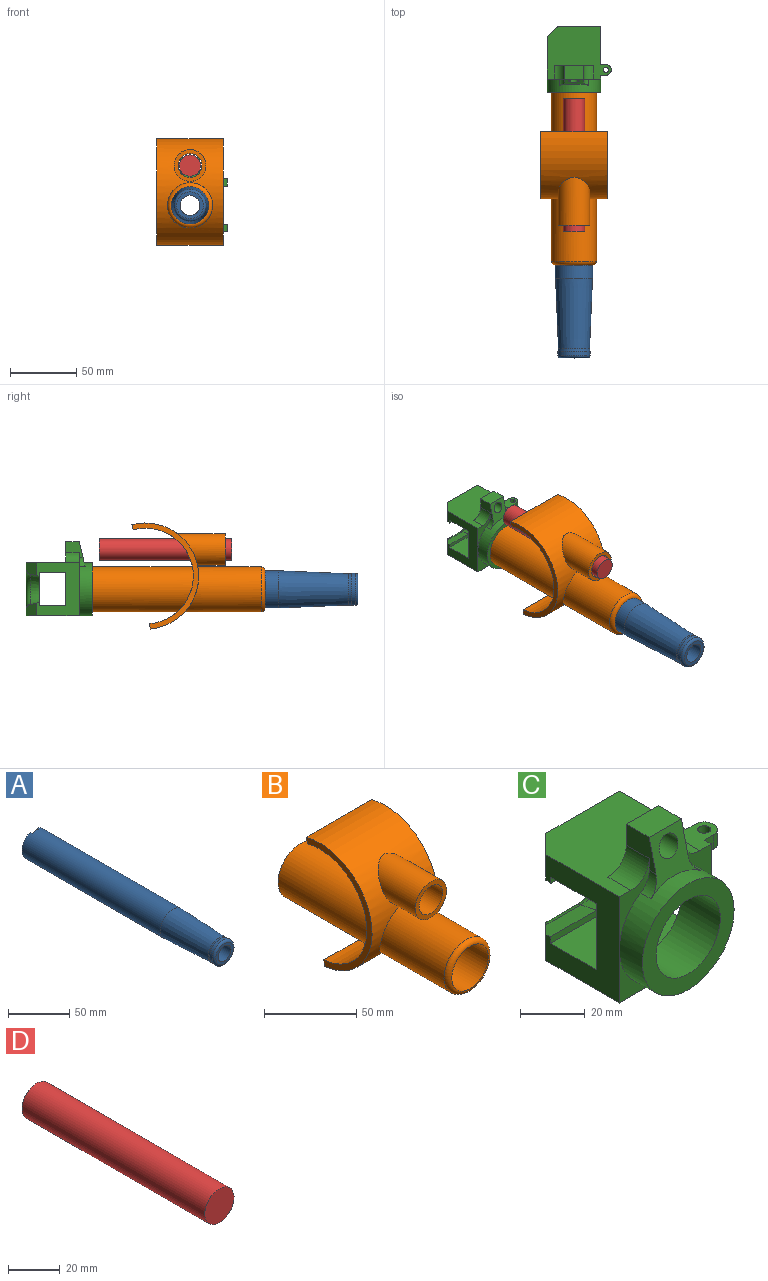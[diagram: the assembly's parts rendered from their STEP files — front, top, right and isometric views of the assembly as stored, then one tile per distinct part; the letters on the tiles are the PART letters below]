
ASSEMBLY  parts=4 mates=3
PART A: 19 faces, bbox 28.7x220x28.7 mm
  f0: plane 26.83x10mm, normal (0,1,0), area 139.7mm2, adj f1,f2,f14,f17
  f1: cylinder r=14mm len=160mm, axis (0,1,0), area 14041.9mm2, adj f0,f3,f4,f13,f14,f15,f16,f17
  f2: cylinder r=9mm len=30mm, axis (0,1,0), area 1663.3mm2, adj f0,f4,f8,f13,f14,f15,f16,f17
  f3: cone r=14mm half-angle=2.4deg, axis (0,1,0), area 4301.6mm2, adj f1,f11
  f4: plane 26.83x10mm, normal (0,1,0), area 139.7mm2, adj f1,f2,f15,f16
  f5: plane 20.2x20.2mm, normal (0,-1,0), area 143.8mm2, adj f6,f12
  f6: cylinder r=7.5mm len=175mm, axis (0,1,0), area 8246.7mm2, adj f5,f10
  f7: cylinder r=12.1mm len=24.2mm, axis (0,-1,0), area 228.1mm2, adj f11,f12
  f8: cone r=9mm half-angle=6.7deg, axis (0,1,0), area 630mm2, adj f2,f9
  f9: cylinder r=7.6mm len=15.2mm, axis (0,1,0), area 143.3mm2, adj f8,f10
  f10: plane 15.2x15.2mm, normal (0,1,0), area 4.7mm2, adj f6,f9
  f11: torus R=16.79mm, axis (0,-1,0), area 148.6mm2, adj f3,f7
  f12: torus R=10.1mm, axis (0,-1,0), area 224.5mm2, adj f5,f7
  f13: plane 8x5.94mm, normal (0,1,0), area 40.9mm2, adj f1,f2,f14,f15
  f14: plane 5.35x2mm, normal (-1,0,0), area 10.7mm2, adj f0,f1,f2,f13
  f15: plane 5.35x2mm, normal (1,0,0), area 10.7mm2, adj f1,f2,f4,f13
  f16: plane 5.35x2mm, normal (1,0,0), area 10.7mm2, adj f1,f2,f4,f18
  f17: plane 5.35x2mm, normal (-1,0,0), area 10.7mm2, adj f0,f1,f2,f18
  f18: plane 8x5.94mm, normal (0,1,0), area 40.9mm2, adj f1,f2,f16,f17
PART B: 14 faces, bbox 50x130x79.8 mm
  f0: cylinder r=17mm len=57.49mm, axis (0,1,0), area 5380.1mm2, adj f1,f2
  f1: torus R=14mm, axis (0,-1,0), area 471.1mm2, adj f0,f12
  f2: cylinder r=40mm len=79.85mm, axis (-1,0,0), area 5123mm2, adj f0,f4,f5,f6,f7,f10
  f3: cylinder r=36mm len=71.86mm, axis (-1,0,0), area 4666.7mm2, adj f4,f5,f6,f7,f9,f13
  f4: plane 50x3.86mm, normal (0,0.97,-0.26), area 200mm2, adj f2,f3,f6,f7
  f5: plane 50x3.98mm, normal (0,1,-0.09), area 200mm2, adj f2,f3,f6,f7
  f6: plane 79.85x50.35mm, normal (1,0,0), area 504.1mm2, adj f2,f3,f4,f5
  f7: plane 79.85x50.35mm, normal (-1,0,0), area 504.1mm2, adj f2,f3,f4,f5
  f8: plane 34x34mm, normal (0,1,0), area 292.2mm2, adj f9,f12
  f9: cylinder r=17mm len=76mm, axis (0,1,0), area 7705.6mm2, adj f3,f8
  f10: cylinder r=12mm len=36mm, axis (0,-1,0), area 2024mm2, adj f2,f11
  f11: plane 24x24mm, normal (0,-1,0), area 197.9mm2, adj f10,f13
  f12: cylinder r=14mm len=130mm, axis (0,1,0), area 11435.4mm2, adj f1,f8
  f13: cylinder r=9mm len=38.67mm, axis (0,-1,0), area 1759.1mm2, adj f3,f11
PART C: 52 faces, bbox 48x50x56 mm
  f0: plane 40x29mm, normal (1,0,0), area 652.1mm2, adj f4,f5,f8,f13,f14,f24,f37,f41
  f1: plane 40x7mm, normal (1,0,0), area 236mm2, adj f8,f11,f12,f13,f37,f39,f41,f44
  f2: plane 3.3x1.17mm, normal (0,-1,0), area 2.2mm2, adj f5,f6,f38
  f3: plane 3.3x1.17mm, normal (0,-1,0), area 2.2mm2, adj f4,f6,f40
  f4: plane 40x20mm, normal (0,0,1), area 587.8mm2, adj f0,f3,f10,f17,f24,f40,f42
  f5: plane 40x20mm, normal (0,0,-1), area 587.8mm2, adj f0,f2,f10,f17,f24,f38,f43
  f6: cylinder r=14mm len=28mm, axis (0,-1,0), area 1609.2mm2, adj f2,f3,f16,f17,f38,f39,f40
  f7: plane 28x13mm, normal (0,-1,0), area 93mm2, adj f8,f9,f10,f28,f31,f33
  f8: plane 48x40mm, normal (0,0,1), area 1312.6mm2, adj f0,f1,f7,f10,f12,f14,f25,f31
  f9: cylinder r=20mm len=40mm, axis (0,1,0), area 1164.8mm2, adj f7,f11,f12,f15,f16,f27,f33,f34
  f10: plane 40x32mm, normal (-1,0,0), area 739.2mm2, adj f4,f5,f7,f8,f13,f15,f17,f18
  f11: plane 20x20mm, normal (0,-1,0), area 85.8mm2, adj f1,f9,f13
  f12: plane 28x13mm, normal (0,-1,0), area 93mm2, adj f1,f8,f9,f29,f32,f34
  f13: plane 48x40mm, normal (0,0,-1), area 1612.6mm2, adj f0,f1,f10,f11,f14,f15,f35,f48
  f14: plane 40x32mm, normal (0,1,0), area 546.6mm2, adj f0,f8,f13,f21,f22,f23,f35,f36
  f15: plane 20x20mm, normal (0,-1,0), area 85.8mm2, adj f9,f10,f13
  f16: plane 40x40mm, normal (0,-1,0), area 640.9mm2, adj f6,f9
  f17: plane 25x13.7mm, normal (0,1,0), area 204.9mm2, adj f4,f5,f6,f10
  f18: plane 20x6.78mm, normal (0,0.2,0.98), area 126.7mm2, adj f10,f19,f23,f24,f35
  f19: cone r=10mm half-angle=11.3deg, axis (0,1,0), area 232.1mm2, adj f18,f20,f22,f24
  f20: plane 20x6.78mm, normal (0,0.2,-0.98), area 126.7mm2, adj f10,f19,f21,f24,f36
  f21: cylinder r=4mm len=15.22mm, axis (1,0,0), area 72.2mm2, adj f14,f20,f22,f36
  f22: torus R=15.28mm, axis (0,-1,0), area 223.3mm2, adj f14,f19,f21,f23
  f23: cylinder r=4mm len=15.22mm, axis (-1,0,0), area 72.2mm2, adj f14,f18,f22,f35
  f24: plane 40x25mm, normal (0,-1,0), area 442.9mm2, adj f0,f4,f5,f10,f18,f19,f20
  f25: plane 30x16mm, normal (0,1,0), area 201.2mm2, adj f8,f26,f28,f29,f30,f31,f32
  f26: plane 14x10mm, normal (0,0,1), area 140mm2, adj f25,f27,f28,f29
  f27: plane 21.43x19.11mm, normal (0,-0.97,0.23), area 192.1mm2, adj f9,f26,f28,f29,f30,f33,f34
  f28: plane 12.94x12.36mm, normal (-1,0,0), area 98.2mm2, adj f7,f25,f26,f27,f31,f33
  f29: plane 12.94x12.36mm, normal (1,0,0), area 98.2mm2, adj f12,f25,f26,f27,f32,f34
  f30: cylinder r=4mm len=12.38mm, axis (0,-1,0), area 287.2mm2, adj f25,f27
  f31: cylinder r=8mm len=10mm, axis (0,1,0), area 125.7mm2, adj f7,f8,f25,f28
  f32: cylinder r=8mm len=10mm, axis (0,-1,0), area 125.7mm2, adj f8,f12,f25,f29
  f33: cylinder r=8mm len=6.76mm, axis (0,1,0), area 30.7mm2, adj f7,f9,f27,f28
  f34: cylinder r=8mm len=6.76mm, axis (0,1,0), area 30.7mm2, adj f9,f12,f27,f29
  f35: plane 9.6x8mm, normal (-0.71,0.71,0), area 96.5mm2, adj f10,f13,f14,f18,f23
  f36: plane 9.6x8mm, normal (-0.71,0.71,0), area 96.5mm2, adj f8,f10,f14,f20,f21
  f37: plane 31x16.23mm, normal (0,0,-1), area 325.8mm2, adj f0,f1,f38,f39,f43,f44,f45,f46
  f38: plane 12.23x2mm, normal (1,0,0), area 20.9mm2, adj f2,f5,f6,f37,f39,f43
  f39: plane 29x23mm, normal (0,1,0), area 275.8mm2, adj f1,f6,f37,f38,f40,f41
  f40: plane 12.23x2mm, normal (1,0,0), area 20.9mm2, adj f3,f4,f6,f39,f41,f42
  f41: plane 31x16.23mm, normal (0,0,1), area 325.8mm2, adj f0,f1,f39,f40,f42,f48,f49,f50
  f42: plane 23x2mm, normal (0,-1,0), area 46mm2, adj f0,f4,f40,f41
  f43: plane 23x2mm, normal (0,-1,0), area 46mm2, adj f0,f5,f37,f38
  f44: plane 5.5x4mm, normal (0,-1,0), area 22mm2, adj f1,f8,f37,f47
  f45: plane 5.5x4mm, normal (0,1,0), area 22mm2, adj f0,f8,f37,f47
  f46: cylinder r=2mm len=5.5mm, axis (0,0,-1), area 69.1mm2, adj f8,f37
  f47: cylinder r=4mm len=8mm, axis (0,0,-1), area 69.1mm2, adj f8,f37,f44,f45
  f48: plane 5.5x4mm, normal (0,-1,0), area 22mm2, adj f1,f13,f41,f50
  f49: plane 5.5x4mm, normal (0,1,0), area 22mm2, adj f0,f13,f41,f50
  f50: cylinder r=4mm len=8mm, axis (0,0,1), area 69.1mm2, adj f13,f41,f48,f49
  f51: cylinder r=2mm len=5.5mm, axis (0,0,1), area 69.1mm2, adj f13,f41
PART D: 7 faces, bbox 16x100x16 mm
  f0: cylinder r=2mm len=5mm, axis (0,-1,0), area 62.8mm2, adj f1,f6
  f1: plane 16x16mm, normal (0,1,0), area 188.5mm2, adj f0,f2
  f2: cylinder r=8mm len=100mm, axis (0,-1,0), area 5026.5mm2, adj f1,f3
  f3: plane 16x16mm, normal (0,-1,0), area 201.1mm2, adj f2
  f4: plane 12x12mm, normal (0,1,0), area 113.1mm2, adj f5
  f5: cylinder r=6mm len=90mm, axis (0,-1,0), area 3392.9mm2, adj f4,f6
  f6: plane 12x12mm, normal (0,-1,0), area 100.5mm2, adj f0,f5
PLACE A rot(axis=(0.32,-0.51,-0.8),0deg) t=(-12.25,-25.14,-21.58)mm
PLACE B t=(-12.25,-85.14,-11.58)mm fixed
PLACE C rot(axis=(0.32,-0.51,-0.8),0deg) t=(-12.25,-35.14,-21.58)mm
PLACE D t=(-12.25,-50.14,8.42)mm
MATE fastened A.f1 <-> C.f6  axis (0,1,0) through (-12.25,-25.14,-21.58)mm
MATE slider B.f0 <-> A.f1  axis (0,1,0) through (-12.25,-45.14,-21.58)mm
MATE fastened D.f0 <-> B.f10  axis (0,-1,0) through (-12.25,-150.14,8.42)mm
